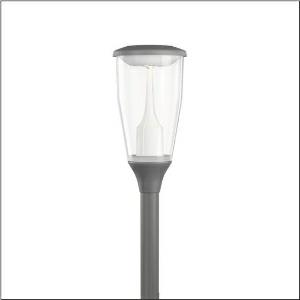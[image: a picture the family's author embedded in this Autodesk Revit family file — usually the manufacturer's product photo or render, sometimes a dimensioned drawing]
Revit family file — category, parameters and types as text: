
# Revit family: dl_11_iq___p1_0a_5xa5575lf14h000022_ea02
name_source: partatom
category: Lighting Fixtures
units: mm (PartAtom-declared; Revit-internal decimal feet)

## family parameters
Cut with Voids When Loaded = No
Host = Face
Light Source = No
Part Type = Normal
Room Calculation Point = No
Round Connector Dimension = Use Diameter
Shared = No

## types (1)
- --- (1 x LED, 1530 lm, 10 W, 4000K)
    Apparent Load = 10 VA
    CIE Flux Codes = 34 63 91 95 100
    Color Rendering = 70
    Color Temperature = 4000K
    Default Elevation = 1800 mm
    Description = DL 11 iQ, mast luminaire, Module 540 iQ-SR, primary light control with 3 zone facetted reflector, of plastic, silver coated, highly specular, structured, primary optical cover: cover, of PMMA, transparent, light distribution: P1.0a, light emission: direct distribution, primary light characteristic: asymmetric, installation type: post-top, LED, High Power LED, light colour: 740, colour temperature: 4000K, control gear: iQ Street-Remote, control: Street-Remote, Auto-Match, Temp-Guard, Lumen-Switch, Night-Set, Smart-Wire, Light-Fading, Desk-Remote (wireless, voltage-free reading and setting of iQ features in the workshop via application-optimized NFC function/RFID function), optimised constant luminous flux control (CLO 2.0), mains connection: 220..240V, AC, 50/60Hz, connection cable pre-assembled, cable length: 5,5m, start of lifetime: 10W, end of service life: 10W, luminaire housing, upper part, of diecast aluminium, coated, SITECO metallic grey (DB 702S), spigot size: 76mm (post-top), mounting height: 3..5m, post-top mast mounting element, of diecast aluminium, coated, SITECO metallic grey (DB 702S), Module 540 iQ-SR, traffic white (RAL 9016), equipment: standard, protection rating (complete): IP66, insulation class (complete): insulation class II (safety insulation), certification: CE, ENEC, ENEC+, VDE, impact resistance: IK07, packaging unit: 1 piece

Light Distribution: P1.0a
    Height = 665 mm
    Lamp = 1 x LED
    Lamp Light Flux = 1530 lm
    Lamp Power = 10 W
    Lamp count = 1
    Length = 334 mm
    Luminous efficacy = 153 lm/W
    Manufacturer = Siteco
    ModVariant = No
    Model = 5XA5575LF14H000022
    Number of Poles = 1
    OnlyDefault = Yes
    Power Factor = 1
    Product Name = DL 11 iQ | P1.0a
    Product group = mast luminaire | pylon top
    ProductGroupID = 6100
    Protection Class = Protection class II
    Protection Degree = IP 66
    RLX_Detail_Level = 1
    RLX_Emergency_Light_Flux = 0 lm
    RLX_Emergency_Type = 0
    RLX_Emergency_Type_DB = No
    RlxData = <blob elided: 108733 chars, md5=2d2a58ba>
    Socket = socket
    Standby Power = 0 W
    System Light Flux = 1530 lm
    System Power = 10 W
    Type Comments = factory setting: luminous flux: 100 % | dim-lin: 254 | 401 mA
    Type Image = l_1258354.jpg
    URL = http://relux.com
    VarID = @adj_095583
    Voltage = 0 V
    Weight = 0.00 kg
    Width = 0 mm  [stored 0 ft]

note: [stored X ft] marks values corroborated as IEEE doubles in the binary element streams (Revit-internal decimal feet)

## geometry (parser evidence)
native form markers: Blend x4, Sweep x8
no freeform markers — native parametric forms only
